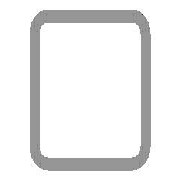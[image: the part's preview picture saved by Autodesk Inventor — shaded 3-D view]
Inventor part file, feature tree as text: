
AUTODESK INVENTOR PART (.ipt)
format: ipt  version: 2025.3 (Build 293356000, 356)  size: 154,112 bytes
history: native  units: mm (DEFAULTED — no unit token found)
features: other x4, plane x3, split x2, sketch x1
ambient origin geometry x8: Origin, YZ Plane, XZ Plane, XY Plane, X Axis, Y Axis, Z Axis, Center Point
bodies: Solid1 (feature_tree), Body (feature_tree)
feature tree (10):
  parser-record x1  (decoder bookkeeping rows leaked as tree rows — omitted from the tree; the rows remain in map.json)
  other  "Driven Length"
  other  "Start Plane"
  other  "End Plane"
  plane  "Work Plane4"
  split  "Split1"
  plane  "Work Plane5"
  split  "Split2"
  sketch  "Sketch3"  dims[d3=2216.344931mm d4=0.0mm d7=6.0mm d9=80.0mm d11=80.0mm d12=3.0mm d13=-14.545455mm d14=2201.799476mm d15=40.0mm d16=40.0mm d17=90.0deg d18=2216.344931mm]
  plane  "Work Plane3"
